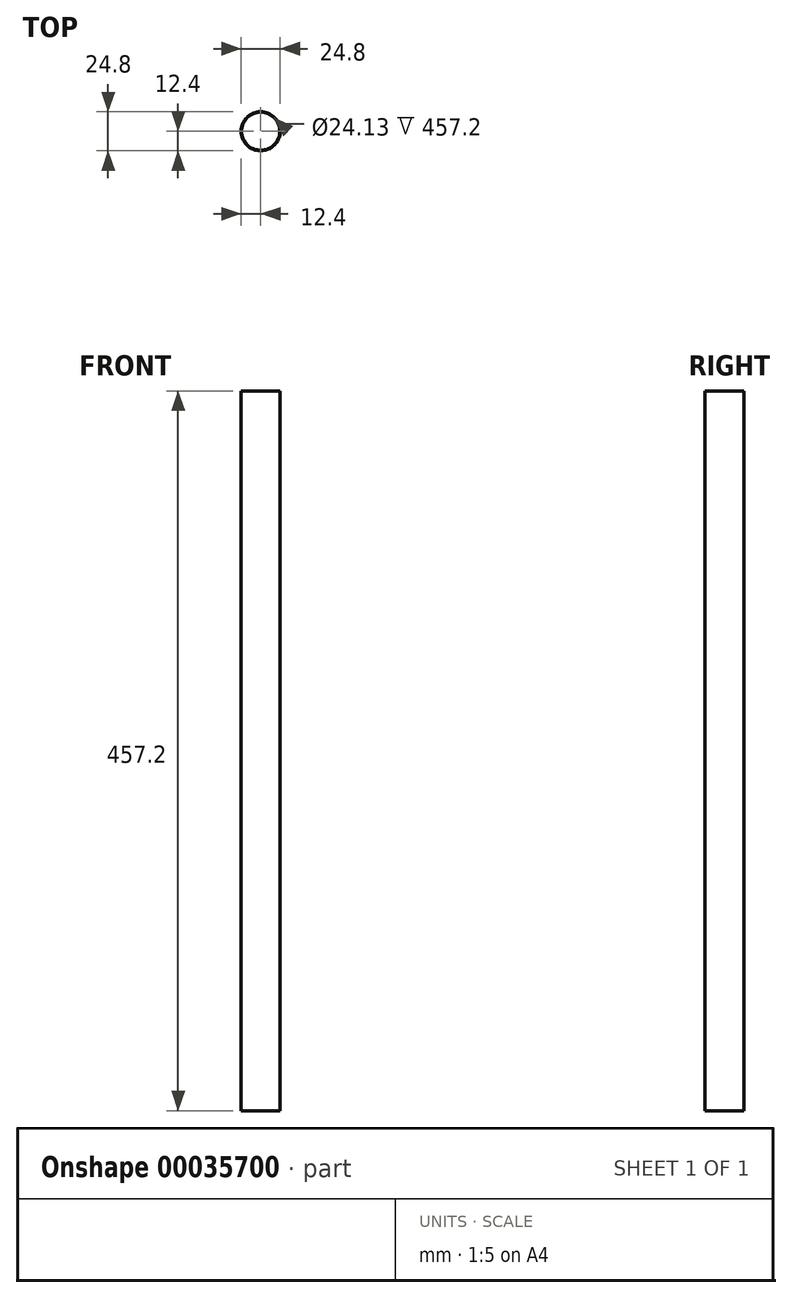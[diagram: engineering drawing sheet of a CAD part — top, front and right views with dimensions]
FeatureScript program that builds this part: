
annotation { "Feature Type Name" : "Feature", "Feature Type Description" : "" }
export const myFeature = defineFeature(function(context is Context, id is Id, definition is map)
    precondition{}
    {
        {
            var Q0;
            Q0=qCreatedBy(makeId("Front.planeOp"),FACE);
            var sketch = newSketch(context, id + "F0", { "sketchPlane" : qUnion([Q0])});
            skLineSegment(sketch, "E0", {"start": v(0, 0) * mm, "end": v(0, 457.2) * mm});
            skLineSegment(sketch, "E1", {"start": v(0, 457.2) * mm, "end": v(12.06, 457.2) * mm});
            skLineSegment(sketch, "E2", {"start": v(12.06, 457.2) * mm, "end": v(12.07, 0) * mm});
            skLineSegment(sketch, "E3", {"start": v(12.07, 0) * mm, "end": v(0, 0) * mm});
            skLineSegment(sketch, "E4", {"start": v(12.07, 0) * mm, "end": v(12.4, 0) * mm});
            skLineSegment(sketch, "E5", {"start": v(12.4, 0) * mm, "end": v(12.4, 457.2) * mm});
            skLineSegment(sketch, "E6", {"start": v(12.4, 457.2) * mm, "end": v(12.06, 457.2) * mm});
            skSolve(sketch);
        }
        {
            var Q0;
            Q0=makeQuery(id+"F0.imprint","IMPRINT",FACE,{"disambiguationData":[TD([[makeQuery(id+"F0.imprint","IMPRINT",EDGE,{"derivedFrom":sQuery(id+"F0.wireOp",EDGE,"E2")}),1.0]])]});
            var Q1;
            Q1=sQuery(id+"F0.wireOp",EDGE,"E0");
            revolve(context, id + "F1", {"entities" : qUnion([Q0]), "axis" : qUnion([Q1]), "revolveType" : RevolveType.FULL});
        }
        {
            var Q0;
            Q0=qCreatedBy(makeId("Top.planeOp"),FACE);
            var sketch = newSketch(context, id + "F2", { "sketchPlane" : qUnion([Q0])});
            skCircle(sketch, "E7.0", {"center": v(0, 0) * mm, "radius": 12.4 * mm});
            skLineSegment(sketch, "E8", {"start": v(0, 0) * mm, "end": v(0, 12.4) * mm});
            skLineSegment(sketch, "E9", {"start": v(0, 0) * mm, "end": v(0, -12.4) * mm});
            skLineSegment(sketch, "E10", {"start": v(0, 0) * mm, "end": v(10.73, -6.2) * mm});
            skLineSegment(sketch, "E11.MirrorCS", {"start": v(0, 0) * mm, "end": v(-10.73, -6.2) * mm});
            skSolve(sketch);
        }
    });
